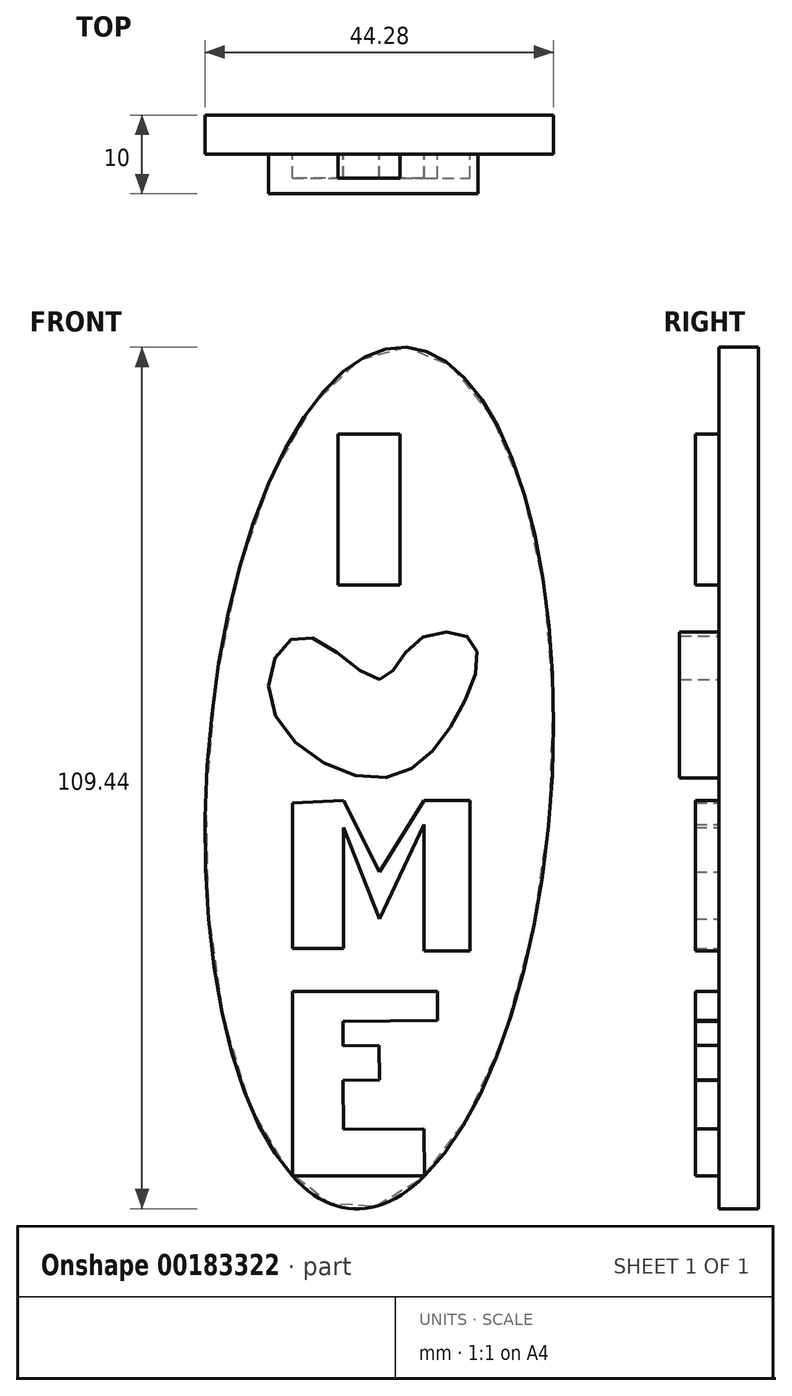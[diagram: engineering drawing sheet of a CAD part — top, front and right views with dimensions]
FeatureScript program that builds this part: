
annotation { "Feature Type Name" : "Feature", "Feature Type Description" : "" }
export const myFeature = defineFeature(function(context is Context, id is Id, definition is map)
    precondition{}
    {
        {
            var Q0;
            Q0=qCreatedBy(makeId("Front.planeOp"),FACE);
            var sketch = newSketch(context, id + "F0", { "sketchPlane" : qUnion([Q0])});
            skEllipse(sketch, "E0", {"center": v(0, 0) * mm, "majorRadius": 54.81 * mm, "minorRadius": 21.92 * mm, "majorAxis": v(0.06, 1)});
            skSolve(sketch);
        }
        {
            var Q0;
            Q0 = qSketchRegion(id + "F0", true);
            extrude(context, id + "F1", {"entities" : qUnion([Q0]), "depth" : 5 * mm});
        }
        {
            var Q0;
            Q0=makeQuery(id+"F1.opExtrude","CAP_FACE",FACE,{"disambiguationData":[OSD([sQuery(id+"F0.wireOp",EDGE,"E0")])],"isStart":false});
            var sketch = newSketch(context, id + "F2", { "sketchPlane" : qUnion([Q0])});
            skFitSpline(sketch, "E1", {"points": [v(0, 12.53) * mm, v(-9.7, 18) * mm, v(-13.8, 9.45) * mm, v(0, 0) * mm, v(9.8, 7.75) * mm, v(11.85, 17.32) * mm, v(4.67, 17.32) * mm, v(0, 12.53) * mm]});
            skSolve(sketch);
        }
        {
            var Q0;
            Q0 = qSketchRegion(id + "F2", true);
            extrude(context, id + "F3", {"entities" : qUnion([Q0]), "operationType" : NewBodyOperationType.ADD, "depth" : 5 * mm});
        }
        {
            var Q0;
            Q0=makeQuery(id+"F1.opExtrude","CAP_FACE",FACE,{"disambiguationData":[OSD([sQuery(id+"F0.wireOp",EDGE,"E0")])],"isStart":false});
            var sketch = newSketch(context, id + "F4", { "sketchPlane" : qUnion([Q0])});
            skLineSegment(sketch, "E2", {"start": v(-5.25, 43.65) * mm, "end": v(-5.25, 24.5) * mm});
            skLineSegment(sketch, "E3", {"start": v(-5.25, 24.5) * mm, "end": v(2.62, 24.5) * mm});
            skLineSegment(sketch, "E4", {"start": v(-5.25, 43.65) * mm, "end": v(2.62, 43.65) * mm});
            skLineSegment(sketch, "E5", {"start": v(2.62, 43.65) * mm, "end": v(2.62, 24.5) * mm});
            skSolve(sketch);
        }
        {
            var Q0;
            Q0 = qSketchRegion(id + "F4", true);
            extrude(context, id + "F5", {"entities" : qUnion([Q0]), "operationType" : NewBodyOperationType.ADD, "depth" : 3 * mm});
        }
        {
            var Q0;
            Q0=makeQuery(id+"F1.opExtrude","CAP_FACE",FACE,{"disambiguationData":[OSD([sQuery(id+"F0.wireOp",EDGE,"E0")])],"isStart":false});
            var sketch = newSketch(context, id + "F6", { "sketchPlane" : qUnion([Q0])});
            skLineSegment(sketch, "E6", {"start": v(-11.06, -3.2) * mm, "end": v(-11.06, -21.67) * mm});
            skLineSegment(sketch, "E7", {"start": v(-11.06, -21.67) * mm, "end": v(-4.56, -21.67) * mm});
            skLineSegment(sketch, "E8", {"start": v(-4.56, -21.67) * mm, "end": v(-4.56, -6.28) * mm});
            skLineSegment(sketch, "E9", {"start": v(-4.56, -6.28) * mm, "end": v(0, -17.9) * mm});
            skLineSegment(sketch, "E10", {"start": v(0, -17.9) * mm, "end": v(5.7, -5.93) * mm});
            skLineSegment(sketch, "E11", {"start": v(5.7, -5.93) * mm, "end": v(5.7, -22) * mm});
            skLineSegment(sketch, "E12", {"start": v(5.7, -22) * mm, "end": v(11.51, -22) * mm});
            skLineSegment(sketch, "E13", {"start": v(11.51, -22) * mm, "end": v(11.51, -2.85) * mm});
            skLineSegment(sketch, "E14", {"start": v(11.51, -2.85) * mm, "end": v(5.7, -2.85) * mm});
            skLineSegment(sketch, "E15", {"start": v(5.7, -2.85) * mm, "end": v(0, -11.92) * mm});
            skPoint(sketch, "E15.endSnap0", {"position": v(2.85, -11.92) * mm});
            skLineSegment(sketch, "E16", {"start": v(0, -11.92) * mm, "end": v(-4.56, -2.85) * mm});
            skLineSegment(sketch, "E17", {"start": v(-4.56, -2.85) * mm, "end": v(-11.06, -3.2) * mm});
            skLineSegment(sketch, "E18", {"start": v(-11.06, -27.13) * mm, "end": v(-11.06, -50.56) * mm});
            skLineSegment(sketch, "E19", {"start": v(-11.06, -50.56) * mm, "end": v(5.75, -50.56) * mm});
            skLineSegment(sketch, "E20", {"start": v(5.75, -50.56) * mm, "end": v(5.7, -44.58) * mm});
            skLineSegment(sketch, "E21", {"start": v(5.7, -44.58) * mm, "end": v(-4.56, -44.67) * mm});
            skLineSegment(sketch, "E22", {"start": v(-4.56, -44.67) * mm, "end": v(-4.62, -38.43) * mm});
            skLineSegment(sketch, "E23", {"start": v(-4.62, -38.43) * mm, "end": v(0, -38.39) * mm});
            skLineSegment(sketch, "E24", {"start": v(0, -38.39) * mm, "end": v(-0.04, -33.97) * mm});
            skLineSegment(sketch, "E25", {"start": v(-0.04, -33.97) * mm, "end": v(-4.62, -34.01) * mm});
            skLineSegment(sketch, "E26", {"start": v(-4.62, -34.01) * mm, "end": v(-4.65, -30.9) * mm});
            skLineSegment(sketch, "E27", {"start": v(-4.65, -30.9) * mm, "end": v(7.41, -30.8) * mm});
            skLineSegment(sketch, "E28", {"start": v(7.41, -30.8) * mm, "end": v(7.38, -27.13) * mm});
            skLineSegment(sketch, "E29", {"start": v(-11.06, -27.13) * mm, "end": v(7.38, -27.13) * mm});
            skSolve(sketch);
        }
        {
            var Q0;
            Q0 = qSketchRegion(id + "F6", true);
            extrude(context, id + "F7", {"entities" : qUnion([Q0]), "operationType" : NewBodyOperationType.ADD, "depth" : 3 * mm});
        }
    });
